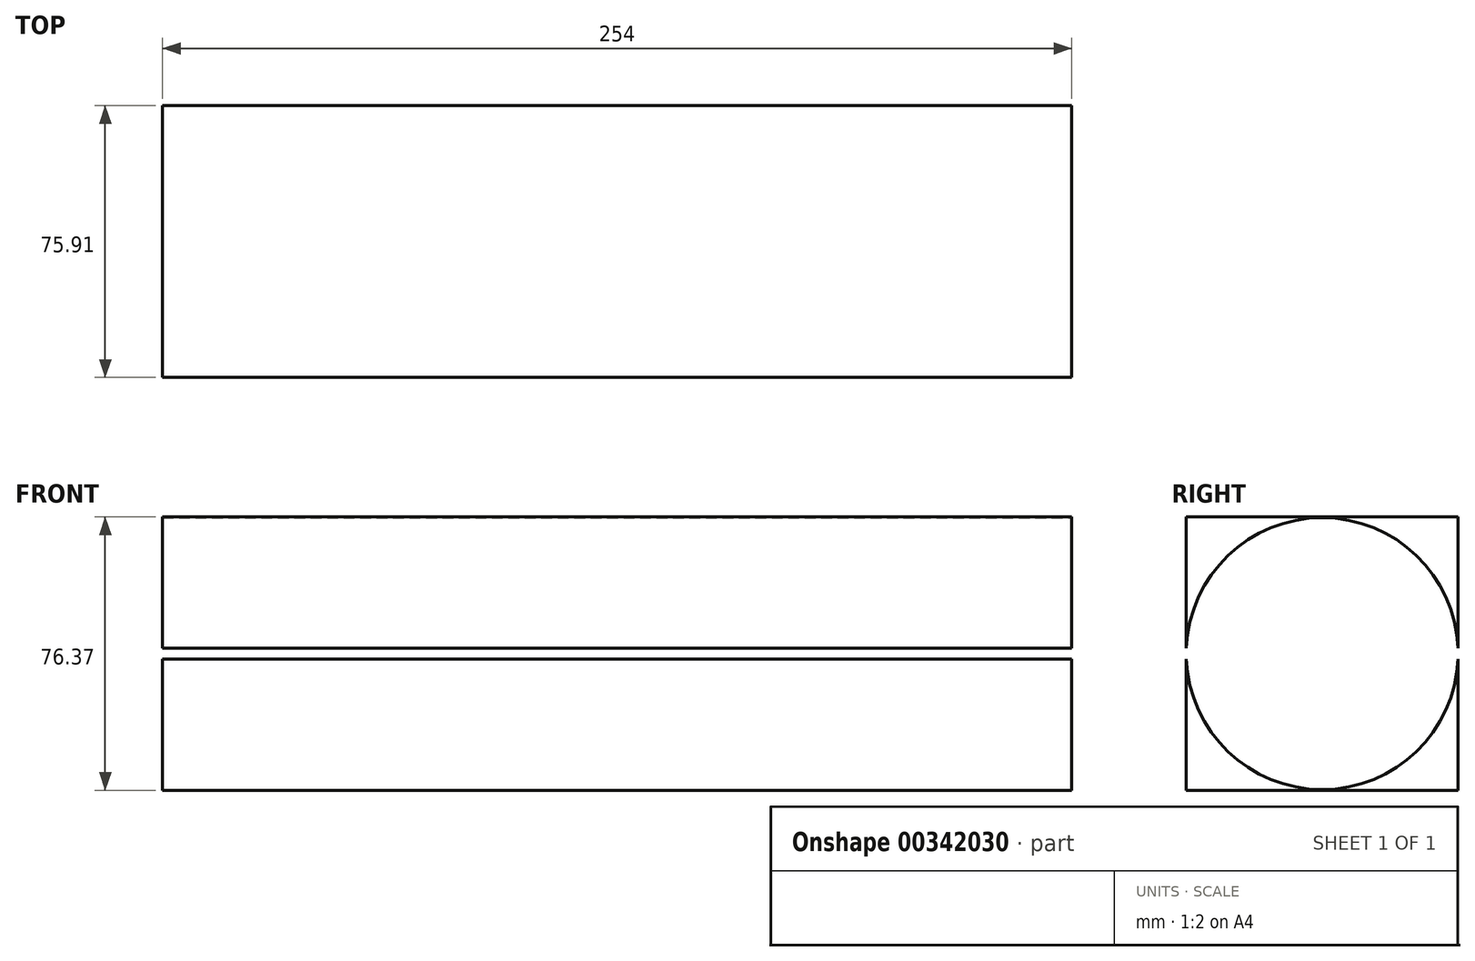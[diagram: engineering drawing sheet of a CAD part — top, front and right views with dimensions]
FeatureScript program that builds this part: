
annotation { "Feature Type Name" : "Feature", "Feature Type Description" : "" }
export const myFeature = defineFeature(function(context is Context, id is Id, definition is map)
    precondition{}
    {
        {
            var Q0;
            Q0=qCreatedBy(makeId("Right.planeOp"),FACE);
            var sketch = newSketch(context, id + "F0", { "sketchPlane" : qUnion([Q0])});
            skLineSegment(sketch, "E0.bottom", {"start": v(0, 0) * mm, "end": v(75.91, 0) * mm});
            skLineSegment(sketch, "E0.top", {"start": v(0, 76.37) * mm, "end": v(75.91, 76.37) * mm});
            skLineSegment(sketch, "E0.left", {"start": v(0, 0) * mm, "end": v(0, 76.37) * mm});
            skLineSegment(sketch, "E0.right", {"start": v(75.91, 0) * mm, "end": v(75.91, 76.37) * mm});
            skSolve(sketch);
        }
        {
            var Q0;
            Q0 = qSketchRegion(id + "F0", true);
            extrude(context, id + "F1", {"entities" : qUnion([Q0]), "depth" : 254 * mm});
        }
        {
            var Q0;
            Q0=makeQuery(id+"F1.opExtrude","CAP_FACE",FACE,{"disambiguationData":[OSD([sQuery(id+"F0.wireOp",EDGE,"E0.bottom"),sQuery(id+"F0.wireOp",EDGE,"E0.top"),sQuery(id+"F0.wireOp",EDGE,"E0.left"),sQuery(id+"F0.wireOp",EDGE,"E0.right")])],"isStart":false});
            var sketch = newSketch(context, id + "F2", { "sketchPlane" : qUnion([Q0])});
            skLineSegment(sketch, "E1", {"start": v(37.96, 76.37) * mm, "end": v(37.96, 0) * mm});
            skCircle(sketch, "E2", {"center": v(37.96, 38.18) * mm, "radius": 37.99 * mm});
            skSolve(sketch);
        }
        {
            var Q0;
            Q0 = qSketchRegion(id + "F2", true);
            extrude(context, id + "F3", {"entities" : qUnion([Q0]), "operationType" : NewBodyOperationType.REMOVE, "oppositeDirection" : true, "depth" : 254 * mm});
        }
    });
